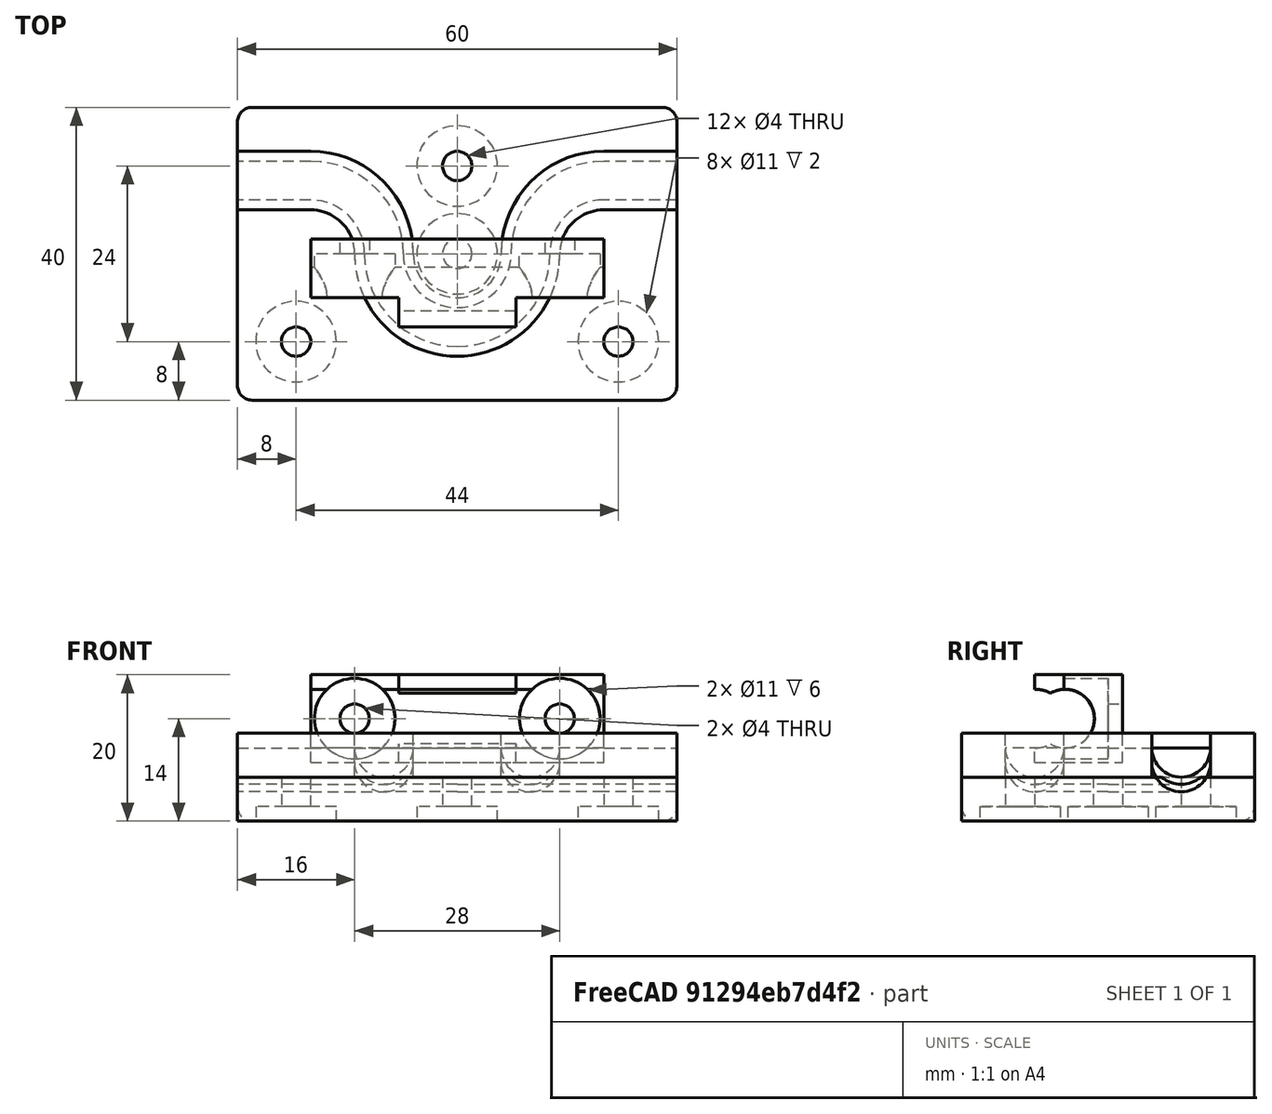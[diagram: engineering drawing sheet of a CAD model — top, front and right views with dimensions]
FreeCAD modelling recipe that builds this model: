
FCSTD DOCUMENT  (FreeCAD 1.0R39109 (Git))
Label: WireHolder220
License: All rights reserved
LicenseURL: https://en.wikipedia.org/wiki/All_rights_reserved
objects: Part::Cylinder×40, Part::Cut×16, Part::MultiFuse×14, Part::Torus×12, Part::Box×10, Part::FeaturePython×8, App::Part×4, Part::Fillet×3
note: 103 computed .brp shape members not serialized (recipe doc carries the construction recipe); baked Part::Feature solids carry a one-line shape summary decoded from their .brp

FEATURE [Part::Box] Box  label="Cube"
  AttacherType = Attacher::AttachEngine3D
  Height = 12
  Length = 60
  Placement = pos=(-10,-10,-8) rot=(0,0,1;0rad)
  Width = 40
FEATURE [Part::Torus] Torus  label="Torus000"
  Angle1 = 0
  Angle2 = 180
  Angle3 = 90
  AttacherType = Attacher::AttachEngine3D
  Placement = pos=(0,10,0) rot=(0,0,1;0rad)
  Radius1 = 10
  Radius2 = 4
FEATURE [Part::Cylinder] Cylinder
  Angle = 180
  AttacherType = Attacher::AttachEngine3D
  FirstAngle = 0
  Height = 10
  Placement = pos=(-10,20,0) rot=(-0.57735,0.57735,-0.57735;2.0944rad)
  Radius = 4
  SecondAngle = 0
FEATURE [Part::Torus] Torus001
  Angle1 = 0
  Angle2 = 180
  Angle3 = 90
  AttacherType = Attacher::AttachEngine3D
  Placement = pos=(20,10,0) rot=(0,0,1;3.14159rad)
  Radius1 = 10
  Radius2 = 4
FEATURE [Part::Torus] Torus002
  Angle1 = 0
  Angle2 = 180
  Angle3 = 90
  AttacherType = Attacher::AttachEngine3D
  Placement = pos=(20,10,0) rot=(0,0,1;4.71239rad)
  Radius1 = 10
  Radius2 = 4
FEATURE [Part::Torus] Torus003
  Angle1 = 0
  Angle2 = 180
  Angle3 = 90
  AttacherType = Attacher::AttachEngine3D
  Placement = pos=(40,10,0) rot=(0,0,1;1.5708rad)
  Radius1 = 10
  Radius2 = 4
FEATURE [Part::Cylinder] Cylinder001
  Angle = 180
  AttacherType = Attacher::AttachEngine3D
  FirstAngle = 0
  Height = 10
  Placement = pos=(40,20,0) rot=(-0.57735,0.57735,-0.57735;2.0944rad)
  Radius = 4
  SecondAngle = 0
FEATURE [Part::FeaturePython] Tube  # WARN: FeaturePython — macro-defined, semantics opaque (R4)
  AttacherType = Attacher::AttachEngine3D
  Height = 10
  InnerRadius = 6
  OuterRadius = 14
  Placement = pos=(0,10,0) rot=(0,0,1;0rad)
FEATURE [Part::Cylinder] Cylinder002
  Angle = 270
  AttacherType = Attacher::AttachEngine3D
  FirstAngle = 0
  Height = 10
  Placement = pos=(0,10,0) rot=(0,0,1;0rad)
  Radius = 14
  SecondAngle = 0
FEATURE [Part::Cut] Cut
  Base = -> Tube
  Placement = pos=(10,10,0) rot=(0,0,1;1.5708rad)
  Tool = -> Cylinder002
FEATURE [Part::Cylinder] Cylinder003
  Angle = 270
  AttacherType = Attacher::AttachEngine3D
  FirstAngle = 0
  Height = 10
  Placement = pos=(0,10,0) rot=(0,0,1;0rad)
  Radius = 14
  SecondAngle = 0
FEATURE [Part::FeaturePython] Tube001  # WARN: FeaturePython — macro-defined, semantics opaque (R4)
  AttacherType = Attacher::AttachEngine3D
  Height = 10
  InnerRadius = 6
  OuterRadius = 14
  Placement = pos=(0,10,0) rot=(0,0,1;0rad)
FEATURE [Part::Cut] Cut001
  Base = -> Tube001
  Placement = pos=(40,20,0) rot=(0,0,1;3.14159rad)
  Tool = -> Cylinder003
FEATURE [Part::Cylinder] Cylinder004
  Angle = 270
  AttacherType = Attacher::AttachEngine3D
  FirstAngle = 0
  Height = 10
  Placement = pos=(0,10,0) rot=(0,0,1;0rad)
  Radius = 14
  SecondAngle = 0
FEATURE [Part::FeaturePython] Tube002  # WARN: FeaturePython — macro-defined, semantics opaque (R4)
  AttacherType = Attacher::AttachEngine3D
  Height = 10
  InnerRadius = 6
  OuterRadius = 14
  Placement = pos=(0,10,0) rot=(0,0,1;0rad)
FEATURE [Part::Cut] Cut002
  Base = -> Tube002
  Placement = pos=(20,0,0) rot=(0,0,1;0rad)
  Tool = -> Cylinder004
FEATURE [Part::Cylinder] Cylinder005
  Angle = 270
  AttacherType = Attacher::AttachEngine3D
  FirstAngle = 0
  Height = 10
  Placement = pos=(0,10,0) rot=(0,0,1;0rad)
  Radius = 14
  SecondAngle = 0
FEATURE [Part::FeaturePython] Tube003  # WARN: FeaturePython — macro-defined, semantics opaque (R4)
  AttacherType = Attacher::AttachEngine3D
  Height = 10
  InnerRadius = 6
  OuterRadius = 14
  Placement = pos=(0,10,0) rot=(0,0,1;0rad)
FEATURE [Part::Cut] Cut003
  Base = -> Tube003
  Placement = pos=(10,10,0) rot=(0,0,1;4.71239rad)
  Tool = -> Cylinder005
FEATURE [Part::Box] Box001  label="Cube001"
  AttacherType = Attacher::AttachEngine3D
  Height = 10
  Length = 10
  Placement = pos=(-10,16,0) rot=(0,0,1;0rad)
  Width = 8
FEATURE [Part::Box] Box002  label="Cube002"
  AttacherType = Attacher::AttachEngine3D
  Height = 10
  Length = 10
  Placement = pos=(40,16,0) rot=(0,0,1;0rad)
  Width = 8
FEATURE [Part::MultiFuse] Fusion
  Shapes = -> [Cut,Cut001,Cut002,Cut003,Box001,Box002]
FEATURE [Part::MultiFuse] Fusion001
  Shapes = -> [Cylinder,Torus,Torus001,Torus002,Torus003,Cylinder001]
FEATURE [Part::Box] Box003  label="Cube003"
  AttacherType = Attacher::AttachEngine3D
  Height = 10
  Length = 10
  Placement = pos=(-10,16,0) rot=(0,0,1;0rad)
  Width = 8
FEATURE [Part::Box] Box004  label="Cube004"
  AttacherType = Attacher::AttachEngine3D
  Height = 10
  Length = 10
  Placement = pos=(40,16,0) rot=(0,0,1;0rad)
  Width = 8
FEATURE [Part::Cylinder] Cylinder006
  Angle = 180
  AttacherType = Attacher::AttachEngine3D
  FirstAngle = 0
  Height = 10
  Placement = pos=(-10,20,0) rot=(-0.57735,0.57735,-0.57735;2.0944rad)
  Radius = 4
  SecondAngle = 0
FEATURE [Part::Cylinder] Cylinder007
  Angle = 180
  AttacherType = Attacher::AttachEngine3D
  FirstAngle = 0
  Height = 10
  Placement = pos=(40,20,0) rot=(-0.57735,0.57735,-0.57735;2.0944rad)
  Radius = 4
  SecondAngle = 0
FEATURE [Part::Cylinder] Cylinder008 .. Cylinder011  x4 (patterned run collapsed; names and placements below)
  Angle = 270
  AttacherType = Attacher::AttachEngine3D
  FirstAngle = 0
  Height = 10
  Radius = 14
  SecondAngle = 0
  placements: all 4 at pos=(0,10,0) rot=(0,0,1;0rad)
FEATURE [Part::Torus] Torus004
  Angle1 = 0
  Angle2 = 180
  Angle3 = 90
  AttacherType = Attacher::AttachEngine3D
  Placement = pos=(0,10,0) rot=(0,0,1;0rad)
  Radius1 = 10
  Radius2 = 4
FEATURE [Part::Torus] Torus005
  Angle1 = 0
  Angle2 = 180
  Angle3 = 90
  AttacherType = Attacher::AttachEngine3D
  Placement = pos=(20,10,0) rot=(0,0,1;3.14159rad)
  Radius1 = 10
  Radius2 = 4
FEATURE [Part::Torus] Torus006
  Angle1 = 0
  Angle2 = 180
  Angle3 = 90
  AttacherType = Attacher::AttachEngine3D
  Placement = pos=(20,10,0) rot=(0,0,1;4.71239rad)
  Radius1 = 10
  Radius2 = 4
FEATURE [Part::Torus] Torus007
  Angle1 = 0
  Angle2 = 180
  Angle3 = 90
  AttacherType = Attacher::AttachEngine3D
  Placement = pos=(40,10,0) rot=(0,0,1;1.5708rad)
  Radius1 = 10
  Radius2 = 4
FEATURE [Part::MultiFuse] Fusion003
  Placement = pos=(0,0,2) rot=(0,0,1;0rad)
  Shapes = -> [Cylinder006,Torus004,Torus005,Torus006,Torus007,Cylinder007]
FEATURE [Part::FeaturePython] Tube004  # WARN: FeaturePython — macro-defined, semantics opaque (R4)
  AttacherType = Attacher::AttachEngine3D
  Height = 10
  InnerRadius = 6
  OuterRadius = 14
  Placement = pos=(0,10,0) rot=(0,0,1;0rad)
FEATURE [Part::Cut] Cut004
  Base = -> Tube004
  Placement = pos=(10,10,0) rot=(0,0,1;1.5708rad)
  Tool = -> Cylinder008
FEATURE [Part::FeaturePython] Tube005  # WARN: FeaturePython — macro-defined, semantics opaque (R4)
  AttacherType = Attacher::AttachEngine3D
  Height = 10
  InnerRadius = 6
  OuterRadius = 14
  Placement = pos=(0,10,0) rot=(0,0,1;0rad)
FEATURE [Part::Cut] Cut005
  Base = -> Tube005
  Placement = pos=(40,20,0) rot=(0,0,1;3.14159rad)
  Tool = -> Cylinder009
FEATURE [Part::FeaturePython] Tube006  # WARN: FeaturePython — macro-defined, semantics opaque (R4)
  AttacherType = Attacher::AttachEngine3D
  Height = 10
  InnerRadius = 6
  OuterRadius = 14
  Placement = pos=(0,10,0) rot=(0,0,1;0rad)
FEATURE [Part::Cut] Cut006
  Base = -> Tube006
  Placement = pos=(20,0,0) rot=(0,0,1;0rad)
  Tool = -> Cylinder010
FEATURE [Part::FeaturePython] Tube007  # WARN: FeaturePython — macro-defined, semantics opaque (R4)
  AttacherType = Attacher::AttachEngine3D
  Height = 10
  InnerRadius = 6
  OuterRadius = 14
  Placement = pos=(0,10,0) rot=(0,0,1;0rad)
FEATURE [Part::Cut] Cut007
  Base = -> Tube007
  Placement = pos=(10,10,0) rot=(0,0,1;4.71239rad)
  Tool = -> Cylinder011
FEATURE [Part::MultiFuse] Fusion002
  Placement = pos=(0,0,-8) rot=(0,0,1;0rad)
  Shapes = -> [Cut004,Cut005,Cut006,Cut007,Box003,Box004]
FEATURE [Part::MultiFuse] Fusion004
  Shapes = -> [Fusion,Fusion001]
FEATURE [Part::Cut] Cut008
  Base = -> Box
  Tool = -> Fusion004
FEATURE [Part::Box] Box005  label="Cube005"
  AttacherType = Attacher::AttachEngine3D
  Height = 6
  Length = 60
  Placement = pos=(-10,-10,-8) rot=(0,0,1;0rad)
  Width = 40
FEATURE [Part::MultiFuse] Fusion005
  Shapes = -> [Box005,Fusion002]
FEATURE [Part::Cut] Cut009
  Base = -> Fusion005
  Tool = -> Fusion003
FEATURE [Part::Cylinder] Cylinder012
  Angle = 360
  AttacherType = Attacher::AttachEngine3D
  FirstAngle = 0
  Height = 12
  Placement = pos=(-2,-2,-8) rot=(0,0,1;0rad)
  Radius = 2
  SecondAngle = 0
FEATURE [Part::Cylinder] Cylinder013
  Angle = 360
  AttacherType = Attacher::AttachEngine3D
  FirstAngle = 0
  Height = 12
  Placement = pos=(42,-2,-8) rot=(0,0,1;0rad)
  Radius = 2
  SecondAngle = 0
FEATURE [Part::Cylinder] Cylinder014
  Angle = 360
  AttacherType = Attacher::AttachEngine3D
  FirstAngle = 0
  Height = 12
  Placement = pos=(20,10,-8) rot=(0,0,1;0rad)
  Radius = 2
  SecondAngle = 0
FEATURE [Part::Cylinder] Cylinder015
  Angle = 360
  AttacherType = Attacher::AttachEngine3D
  FirstAngle = 0
  Height = 12
  Placement = pos=(20,22,-8) rot=(0,0,1;0rad)
  Radius = 2
  SecondAngle = 0
FEATURE [Part::Cylinder] Cylinder016
  Angle = 360
  AttacherType = Attacher::AttachEngine3D
  FirstAngle = 0
  Height = 12
  Placement = pos=(-2,-2,-8) rot=(0,0,1;0rad)
  Radius = 2
  SecondAngle = 0
FEATURE [Part::Cylinder] Cylinder017
  Angle = 360
  AttacherType = Attacher::AttachEngine3D
  FirstAngle = 0
  Height = 12
  Placement = pos=(42,-2,-8) rot=(0,0,1;0rad)
  Radius = 2
  SecondAngle = 0
FEATURE [Part::Cylinder] Cylinder018
  Angle = 360
  AttacherType = Attacher::AttachEngine3D
  FirstAngle = 0
  Height = 12
  Placement = pos=(20,10,-8) rot=(0,0,1;0rad)
  Radius = 2
  SecondAngle = 0
FEATURE [Part::Cylinder] Cylinder019
  Angle = 360
  AttacherType = Attacher::AttachEngine3D
  FirstAngle = 0
  Height = 12
  Placement = pos=(20,22,-8) rot=(0,0,1;0rad)
  Radius = 2
  SecondAngle = 0
FEATURE [Part::MultiFuse] Fusion006
  Shapes = -> [Cylinder012,Cylinder013,Cylinder014,Cylinder015]
FEATURE [Part::Cut] Cut010
  Base = -> Cut008
  Tool = -> Fusion006
FEATURE [Part::Cylinder] Cylinder020
  Angle = 360
  AttacherType = Attacher::AttachEngine3D
  FirstAngle = 0
  Height = 2
  Placement = pos=(-2,-2,-8) rot=(0,0,1;0rad)
  Radius = 5.5
  SecondAngle = 0
FEATURE [Part::Cylinder] Cylinder021
  Angle = 360
  AttacherType = Attacher::AttachEngine3D
  FirstAngle = 0
  Height = 2
  Placement = pos=(42,-2,-8) rot=(0,0,1;0rad)
  Radius = 5.5
  SecondAngle = 0
FEATURE [Part::Cylinder] Cylinder022
  Angle = 360
  AttacherType = Attacher::AttachEngine3D
  FirstAngle = 0
  Height = 2
  Placement = pos=(20,10,-8) rot=(0,0,1;0rad)
  Radius = 5.5
  SecondAngle = 0
FEATURE [Part::Cylinder] Cylinder023
  Angle = 360
  AttacherType = Attacher::AttachEngine3D
  FirstAngle = 0
  Height = 2
  Placement = pos=(20,22,-8) rot=(0,0,1;0rad)
  Radius = 5.5
  SecondAngle = 0
FEATURE [Part::MultiFuse] Fusion007
  Shapes = -> [Cylinder016,Cylinder017,Cylinder018,Cylinder019,Cylinder020,Cylinder021,Cylinder022,Cylinder023]
FEATURE [Part::Cut] Cut011
  Base = -> Cut009
  Tool = -> Fusion007
FEATURE [Part::Fillet] Fillet
  Base = -> Cut011
  EdgeLinks = -> Cut011 [Edge3,Edge4,Edge18,Edge19,Edge21,Edge29,Edge52,Edge53,Edge60,Edge97,Edge98,Edge99]
  Edges = 12 edges r=2: [Edge3,Edge4,Edge18,Edge19,Edge21,Edge29,Edge52,Edge53,Edge60,Edge97,Edge98,Edge99]
FEATURE [App::Part] Part001  label="cover001"
  Group = -> [Cylinder016,Cylinder017,Cylinder018,Cylinder019,Cut009,Fusion005,Box005,Fusion007,Cylinder021,Cylinder010,Cylinder011,Box004,Cut004,Cut005,Box003,Cut006,Cut007,Cylinder006,Cylinder007,Cylinder008,Cylinder009,Torus005,Torus006,Torus007,Tube004,Tube005,Tube006,Tube007,Fusion002,Fusion003,Torus004,Cylinder020,Cylinder022,Cylinder023,Cut011,Fillet]
  Origin = -> Origin001
  Placement = pos=(40,0,15) rot=(0,1,0;3.14159rad)
FEATURE [Part::Fillet] Fillet001
  Base = -> Cut010
  EdgeLinks = -> Cut010 [Edge6,Edge8,Edge35,Edge42]
  Edges = 4 edges r=2: [Edge6,Edge8,Edge35,Edge42]
FEATURE [App::Part] Part  label="base"
  Group = -> [Cut,Fusion004,Fusion,Tube003,Cut003,Cylinder005,Cylinder012,Box002,Tube,Cylinder015,Cylinder,Cylinder004,Tube002,Tube001,Cut002,Torus001,Torus003,Cylinder003,Cut001,Box,Torus,Torus002,Cylinder002,Box001,Fusion006,Cylinder014,Cylinder013,Fusion001,Cylinder001,Cut008,Cut010,Fillet001]
  Origin = -> Origin
  Placement = pos=(0,0,-15) rot=(0,0,1;0rad)
FEATURE [Part::Box] Box008  label="Cube008"
  AttacherType = Attacher::AttachEngine3D
  Height = 6
  Length = 60
  Placement = pos=(-10,-10,-8) rot=(0,0,1;0rad)
  Width = 40
FEATURE [Part::Cylinder] Cylinder024
  Angle = 180
  AttacherType = Attacher::AttachEngine3D
  FirstAngle = 0
  Height = 10
  Placement = pos=(-10,20,0) rot=(-0.57735,0.57735,-0.57735;2.0944rad)
  Radius = 4
  SecondAngle = 0
FEATURE [Part::Cylinder] Cylinder025
  Angle = 180
  AttacherType = Attacher::AttachEngine3D
  FirstAngle = 0
  Height = 10
  Placement = pos=(40,20,0) rot=(-0.57735,0.57735,-0.57735;2.0944rad)
  Radius = 4
  SecondAngle = 0
FEATURE [Part::Cylinder] Cylinder030
  Angle = 360
  AttacherType = Attacher::AttachEngine3D
  FirstAngle = 0
  Height = 12
  Placement = pos=(-2,-2,-8) rot=(0,0,1;0rad)
  Radius = 2
  SecondAngle = 0
FEATURE [Part::Cylinder] Cylinder031
  Angle = 360
  AttacherType = Attacher::AttachEngine3D
  FirstAngle = 0
  Height = 12
  Placement = pos=(42,-2,-8) rot=(0,0,1;0rad)
  Radius = 2
  SecondAngle = 0
FEATURE [Part::Cylinder] Cylinder032
  Angle = 360
  AttacherType = Attacher::AttachEngine3D
  FirstAngle = 0
  Height = 12
  Placement = pos=(20,10,-8) rot=(0,0,1;0rad)
  Radius = 2
  SecondAngle = 0
FEATURE [Part::Cylinder] Cylinder033
  Angle = 360
  AttacherType = Attacher::AttachEngine3D
  FirstAngle = 0
  Height = 12
  Placement = pos=(20,22,-8) rot=(0,0,1;0rad)
  Radius = 2
  SecondAngle = 0
FEATURE [Part::Cylinder] Cylinder034
  Angle = 360
  AttacherType = Attacher::AttachEngine3D
  FirstAngle = 0
  Height = 2
  Placement = pos=(-2,-2,-8) rot=(0,0,1;0rad)
  Radius = 5.5
  SecondAngle = 0
FEATURE [Part::Cylinder] Cylinder035
  Angle = 360
  AttacherType = Attacher::AttachEngine3D
  FirstAngle = 0
  Height = 2
  Placement = pos=(42,-2,-8) rot=(0,0,1;0rad)
  Radius = 5.5
  SecondAngle = 0
FEATURE [Part::Cylinder] Cylinder036
  Angle = 360
  AttacherType = Attacher::AttachEngine3D
  FirstAngle = 0
  Height = 2
  Placement = pos=(20,10,-8) rot=(0,0,1;0rad)
  Radius = 5.5
  SecondAngle = 0
FEATURE [Part::Cylinder] Cylinder037
  Angle = 360
  AttacherType = Attacher::AttachEngine3D
  FirstAngle = 0
  Height = 2
  Placement = pos=(20,22,-8) rot=(0,0,1;0rad)
  Radius = 5.5
  SecondAngle = 0
FEATURE [Part::MultiFuse] Fusion011
  Shapes = -> [Cylinder030,Cylinder031,Cylinder032,Cylinder033,Cylinder034,Cylinder035,Cylinder036,Cylinder037]
FEATURE [Part::Torus] Torus008
  Angle1 = 0
  Angle2 = 180
  Angle3 = 90
  AttacherType = Attacher::AttachEngine3D
  Placement = pos=(0,10,0) rot=(0,0,1;0rad)
  Radius1 = 10
  Radius2 = 4
FEATURE [Part::Torus] Torus009
  Angle1 = 0
  Angle2 = 180
  Angle3 = 90
  AttacherType = Attacher::AttachEngine3D
  Placement = pos=(20,10,0) rot=(0,0,1;3.14159rad)
  Radius1 = 10
  Radius2 = 4
FEATURE [Part::Torus] Torus010
  Angle1 = 0
  Angle2 = 180
  Angle3 = 90
  AttacherType = Attacher::AttachEngine3D
  Placement = pos=(20,10,0) rot=(0,0,1;4.71239rad)
  Radius1 = 10
  Radius2 = 4
FEATURE [Part::Torus] Torus011
  Angle1 = 0
  Angle2 = 180
  Angle3 = 90
  AttacherType = Attacher::AttachEngine3D
  Placement = pos=(40,10,0) rot=(0,0,1;1.5708rad)
  Radius1 = 10
  Radius2 = 4
FEATURE [Part::MultiFuse] Fusion009
  Placement = pos=(0,0,1) rot=(0,0,1;0rad)
  Shapes = -> [Cylinder024,Torus008,Torus009,Torus010,Torus011,Cylinder025]
FEATURE [Part::Cut] Cut012
  Base = -> Box008
  Tool = -> Fusion011
FEATURE [Part::Cut] Cut013
  Base = -> Cut012
  Tool = -> Fusion009
FEATURE [Part::Fillet] Fillet002
  Base = -> Cut013
  EdgeLinks = -> Cut013 [Edge4,Edge5,Edge6,Edge28,Edge29,Edge30,Edge31,Edge36]
  Edges = 8 edges r=2: [Edge4,Edge5,Edge6,Edge28,Edge29,Edge30,Edge31,Edge36]
FEATURE [App::Part] Part002  label="cover002"
  Group = -> [Cut012,Torus009,Torus010,Torus011,Fusion011,Torus008,Cylinder024,Cylinder025,Cylinder030,Cylinder031,Cylinder032,Cylinder033,Cylinder034,Cylinder035,Cylinder036,Cylinder037,Fusion009,Box008,Cut013,Fillet002]
  Origin = -> Origin002
  Placement = pos=(40,0,45) rot=(0,1,0;3.14159rad)
FEATURE [Part::Box] Box009  label="Cube009"
  AttacherType = Attacher::AttachEngine3D
  Height = 12
  Length = 40
  Width = 12
FEATURE [Part::Cylinder] Cylinder038
  Angle = 360
  AttacherType = Attacher::AttachEngine3D
  FirstAngle = 0
  Height = 40
  Placement = pos=(0,4.15,6) rot=(0,1,0;1.5708rad)
  Radius = 4
  SecondAngle = 0
FEATURE [Part::Cylinder] Cylinder039
  Angle = 360
  AttacherType = Attacher::AttachEngine3D
  FirstAngle = 0
  Height = 12
  Placement = pos=(20,12,6) rot=(1,0,0;1.5708rad)
  Radius = 2
  SecondAngle = 0
FEATURE [Part::Cylinder] Cylinder040
  Angle = 360
  AttacherType = Attacher::AttachEngine3D
  FirstAngle = 0
  Height = 10
  Placement = pos=(20,10,6) rot=(1,0,0;1.5708rad)
  Radius = 5.5
  SecondAngle = 0
FEATURE [Part::Box] Box011  label="Cube011"
  AttacherType = Attacher::AttachEngine3D
  Height = 12
  Length = 12
  Placement = pos=(14,0,0) rot=(0,0,1;0rad)
  Width = 4
FEATURE [Part::MultiFuse] Fusion013
  Placement = pos=(-14,0,0) rot=(0,0,1;0rad)
  Shapes = -> [Cylinder039,Cylinder040,Box011]
FEATURE [Part::Box] Box012  label="Cube012"
  AttacherType = Attacher::AttachEngine3D
  Height = 12
  Length = 12
  Placement = pos=(14,0,0) rot=(0,0,1;0rad)
  Width = 4
FEATURE [Part::Cylinder] Cylinder041
  Angle = 360
  AttacherType = Attacher::AttachEngine3D
  FirstAngle = 0
  Height = 12
  Placement = pos=(20,12,6) rot=(1,0,0;1.5708rad)
  Radius = 2
  SecondAngle = 0
FEATURE [Part::Cylinder] Cylinder042
  Angle = 360
  AttacherType = Attacher::AttachEngine3D
  FirstAngle = 0
  Height = 10
  Placement = pos=(20,10,6) rot=(1,0,0;1.5708rad)
  Radius = 5.5
  SecondAngle = 0
FEATURE [Part::MultiFuse] Fusion014
  Placement = pos=(14,0,0) rot=(0,0,1;0rad)
  Shapes = -> [Cylinder041,Cylinder042,Box012]
FEATURE [Part::MultiFuse] Fusion015
  Shapes = -> [Fusion013,Fusion014]
FEATURE [Part::Cylinder] Cylinder043
  Angle = 360
  AttacherType = Attacher::AttachEngine3D
  FirstAngle = 0
  Height = 40
  Placement = pos=(0,0.15,6) rot=(0,1,0;1.5708rad)
  Radius = 4
  SecondAngle = 0
FEATURE [Part::MultiFuse] Fusion016
  Shapes = -> [Cylinder038,Cylinder043]
FEATURE [Part::Cut] Cut014
  Base = -> Box009
  Tool = -> Fusion016
FEATURE [Part::Cut] Cut015
  Base = -> Cut014
  Tool = -> Fusion015
FEATURE [App::Part] Part003  label="clips"
  Group = -> [Box009,Fusion016,Fusion015,Cylinder038,Cylinder043,Cylinder039,Cut014,Box011,Cylinder041,Fusion014,Cylinder042,Fusion013,Box012,Cylinder040,Cut015]
  Origin = -> Origin003
  Placement = pos=(0,0,-50) rot=(0,0,1;0rad)
